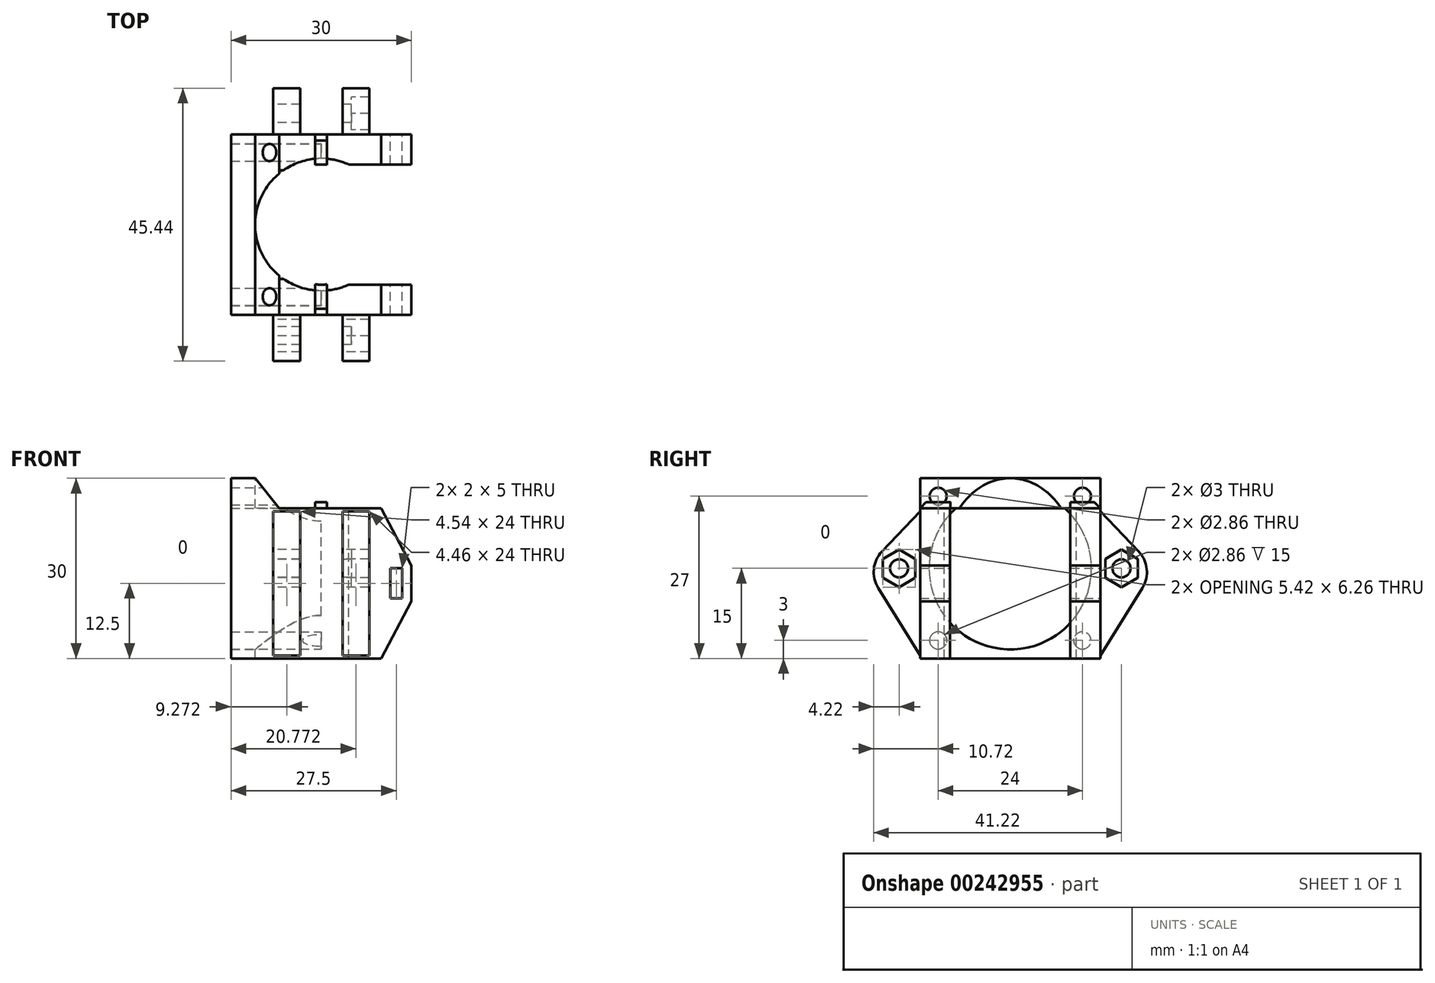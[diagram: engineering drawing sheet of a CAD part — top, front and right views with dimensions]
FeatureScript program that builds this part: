
annotation { "Feature Type Name" : "Feature", "Feature Type Description" : "" }
export const myFeature = defineFeature(function(context is Context, id is Id, definition is map)
    precondition{}
    {
        {
            var Q0;
            Q0=qCreatedBy(makeId("Front.planeOp"),FACE);
            var sketch = newSketch(context, id + "F0", { "sketchPlane" : qUnion([Q0])});
            skLineSegment(sketch, "E0", {"start": v(-15, 15) * mm, "end": v(-15, -15) * mm});
            skLineSegment(sketch, "E1", {"start": v(-15, -15) * mm, "end": v(10, -15) * mm});
            skLineSegment(sketch, "E2", {"start": v(15, -5.5) * mm, "end": v(15, 0.5) * mm});
            skLineSegment(sketch, "E3", {"start": v(10, 10) * mm, "end": v(-7, 10) * mm});
            skLineSegment(sketch, "E4", {"start": v(-11, 15) * mm, "end": v(-15, 15) * mm});
            skLineSegment(sketch, "E5.0", {"start": v(10, -15) * mm, "end": v(10, 10) * mm});
            skLineSegment(sketch, "E6", {"start": v(10, 10) * mm, "end": v(15, 0.5) * mm});
            skLineSegment(sketch, "E7", {"start": v(15, -5.5) * mm, "end": v(10, -15) * mm});
            skLineSegment(sketch, "E8.0", {"start": v(13.5, -5) * mm, "end": v(13.5, 0) * mm});
            skLineSegment(sketch, "E9.0", {"start": v(11.5, -5) * mm, "end": v(11.5, 0) * mm});
            skLineSegment(sketch, "E10.trimOffspring", {"start": v(11.5, 0) * mm, "end": v(13.5, 0) * mm});
            skLineSegment(sketch, "E11.trimOffspring", {"start": v(11.5, -5) * mm, "end": v(13.5, -5) * mm});
            skLineSegment(sketch, "E12", {"start": v(-11, 15) * mm, "end": v(-7, 10) * mm});
            skSolve(sketch);
        }
        {
            var Q0;
            Q0=qCreatedBy(makeId("Top.planeOp"),FACE);
            var sketch = newSketch(context, id + "F1", { "sketchPlane" : qUnion([Q0])});
            skArc(sketch, "E13", {"start": v(4.58, 10) * mm, "mid": v(-11, 0) * mm, "end": v(4.58, -10) * mm});
            skLineSegment(sketch, "E14.0", {"start": v(4.58, -10) * mm, "end": v(16, -10) * mm});
            skLineSegment(sketch, "E15.0", {"start": v(4.58, 10) * mm, "end": v(16, 10) * mm});
            skLineSegment(sketch, "E16", {"start": v(16, 10) * mm, "end": v(16, -10) * mm});
            skSolve(sketch);
        }
        {
            var Q0;
            Q0=qCreatedBy(makeId("Right.planeOp"),FACE);
            var sketch = newSketch(context, id + "F2", { "sketchPlane" : qUnion([Q0])});
            skArc(sketch, "E17", {"start": v(-9.07, 10) * mm, "mid": v(0, -13.5) * mm, "end": v(9.07, 10) * mm});
            skLineSegment(sketch, "E18", {"start": v(-9.07, 10) * mm, "end": v(9.07, 10) * mm});
            skCircle(sketch, "E19", {"center": v(-12, -12) * mm, "radius": 1.43 * mm});
            skCircle(sketch, "E20", {"center": v(-12, 12) * mm, "radius": 1.43 * mm});
            skCircle(sketch, "E21", {"center": v(12, -12) * mm, "radius": 1.43 * mm});
            skCircle(sketch, "E22", {"center": v(12, 12) * mm, "radius": 1.43 * mm});
            skSolve(sketch);
        }
        {
            var Q0;
            Q0=qCreatedBy(makeId("Right.planeOp"),FACE);
            var sketch = newSketch(context, id + "F3", { "sketchPlane" : qUnion([Q0])});
            skLineSegment(sketch, "E23", {"start": v(21.97, -3.26) * mm, "end": v(15, -14.5) * mm});
            skLineSegment(sketch, "E24", {"start": v(21.34, 2.81) * mm, "end": v(15, 9.5) * mm});
            skLineSegment(sketch, "E25", {"start": v(15, 9.5) * mm, "end": v(15, -14.5) * mm});
            skCircle(sketch, "E26", {"center": v(18.5, 0) * mm, "radius": 1.5 * mm});
            skPoint(sketch, "E27.visualSharp", {"position": v(24, 0.02) * mm});
            skArc(sketch, "E27.filletArc", {"start": v(21.97, -3.26) * mm, "mid": v(22.7, -0.12) * mm, "end": v(21.34, 2.81) * mm});
            skLineSegment(sketch, "E28.MirrorCS", {"start": v(-21.34, 2.81) * mm, "end": v(-15, 9.5) * mm});
            skArc(sketch, "E29.MirrorCS", {"start": v(-21.97, -3.26) * mm, "mid": v(-22.7, -0.12) * mm, "end": v(-21.34, 2.81) * mm});
            skLineSegment(sketch, "E30.MirrorCS", {"start": v(-21.97, -3.26) * mm, "end": v(-15, -14.5) * mm});
            skCircle(sketch, "E31.MirrorC", {"center": v(-18.5, 0) * mm, "radius": 1.5 * mm});
            skLineSegment(sketch, "E32.MirrorCS", {"start": v(-15, 9.5) * mm, "end": v(-15, -14.5) * mm});
            skPoint(sketch, "E33.0.midPoint", {"position": v(18.5, 2.5) * mm});
            skCircle(sketch, "E34.cCircle", {"center": v(18.5, 0) * mm, "radius": 2.71 * mm, "construction": true});
            skLineSegment(sketch, "E34.0", {"start": v(21.2, 1.56) * mm, "end": v(21.2, -1.56) * mm});
            skLineSegment(sketch, "E34.1", {"start": v(21.2, -1.56) * mm, "end": v(18.5, -3.13) * mm});
            skLineSegment(sketch, "E34.2", {"start": v(18.5, -3.13) * mm, "end": v(15.8, -1.56) * mm});
            skLineSegment(sketch, "E34.3", {"start": v(15.8, -1.56) * mm, "end": v(15.8, 1.56) * mm});
            skLineSegment(sketch, "E34.4", {"start": v(15.8, 1.56) * mm, "end": v(18.5, 3.13) * mm});
            skLineSegment(sketch, "E34.5", {"start": v(18.5, 3.13) * mm, "end": v(21.2, 1.56) * mm});
            skPoint(sketch, "E34.0.midPoint", {"position": v(21.2, 0) * mm});
            skCircle(sketch, "E35.MirrorC", {"center": v(-18.5, 0) * mm, "radius": 2.71 * mm, "construction": true});
            skLineSegment(sketch, "E36.MirrorCS", {"start": v(-18.5, 3.13) * mm, "end": v(-21.2, 1.56) * mm});
            skLineSegment(sketch, "E37.MirrorCS", {"start": v(-21.2, 1.56) * mm, "end": v(-21.2, -1.56) * mm});
            skLineSegment(sketch, "E38.MirrorCS", {"start": v(-21.2, -1.56) * mm, "end": v(-18.5, -3.13) * mm});
            skLineSegment(sketch, "E39.MirrorCS", {"start": v(-18.5, -3.13) * mm, "end": v(-15.8, -1.56) * mm});
            skLineSegment(sketch, "E40.MirrorCS", {"start": v(-15.8, -1.56) * mm, "end": v(-15.8, 1.56) * mm});
            skLineSegment(sketch, "E41.MirrorCS", {"start": v(-15.8, 1.56) * mm, "end": v(-18.5, 3.13) * mm});
            skSolve(sketch);
        }
        {
            var Q0;
            Q0=qCreatedBy(makeId("Top.planeOp"),FACE);
            var sketch = newSketch(context, id + "F4", { "sketchPlane" : qUnion([Q0])});
            skLineSegment(sketch, "E42", {"start": v(3.54, 15) * mm, "end": v(3.54, 27) * mm});
            skLineSegment(sketch, "E43", {"start": v(3.54, 27) * mm, "end": v(-3.46, 27) * mm});
            skLineSegment(sketch, "E44", {"start": v(-3.46, 27) * mm, "end": v(-3.46, 15) * mm});
            skLineSegment(sketch, "E45", {"start": v(-3.46, 15) * mm, "end": v(3.54, 15) * mm});
            skLineSegment(sketch, "E46.MirrorCS", {"start": v(3.54, -27) * mm, "end": v(-3.46, -27) * mm});
            skLineSegment(sketch, "E47.MirrorCS", {"start": v(3.54, -15) * mm, "end": v(3.54, -27) * mm});
            skLineSegment(sketch, "E48.MirrorCS", {"start": v(-3.46, -27) * mm, "end": v(-3.46, -15) * mm});
            skLineSegment(sketch, "E49.MirrorCS", {"start": v(-3.46, -15) * mm, "end": v(3.54, -15) * mm});
            skSolve(sketch);
        }
        {
            var Q0;
            Q0=makeQuery(id+"F0.imprint","IMPRINT",FACE,{"disambiguationData":[TD([[makeQuery(id+"F0.imprint","IMPRINT",EDGE,{"derivedFrom":sQuery(id+"F0.wireOp",EDGE,"E0")}),1.0]])]});
            var Q1;
            Q1=makeQuery(id+"F0.imprint","IMPRINT",FACE,{"disambiguationData":[TD([[makeQuery(id+"F0.imprint","IMPRINT",EDGE,{"derivedFrom":sQuery(id+"F0.wireOp",EDGE,"E2")}),1.0]])]});
            extrude(context, id + "F5", {"entities" : qUnion([Q0, Q1]), "endBound" : BoundingType.SYMMETRIC, "offsetDistance" : 25 * mm, "depth" : 30 * mm});
        }
        {
            var Q0;
            Q0=makeQuery(id+"F1.imprint","IMPRINT",FACE,{"disambiguationData":[TD([[makeQuery(id+"F1.imprint","IMPRINT",EDGE,{"derivedFrom":sQuery(id+"F1.wireOp",EDGE,"E13")}),1.0]])]});
            extrude(context, id + "F6", {"entities" : qUnion([Q0]), "operationType" : NewBodyOperationType.REMOVE, "endBound" : BoundingType.SYMMETRIC, "oppositeDirection" : true, "depth" : 30 * mm});
        }
        {
            var Q0;
            Q0=makeQuery(id+"F2.imprint","IMPRINT",FACE,{"disambiguationData":[TD([[makeQuery(id+"F2.imprint","IMPRINT",EDGE,{"derivedFrom":sQuery(id+"F2.wireOp",EDGE,"E17")}),1.0]])]});
            extrude(context, id + "F7", {"entities" : qUnion([Q0]), "operationType" : NewBodyOperationType.REMOVE, "oppositeDirection" : true, "depth" : 16 * mm});
        }
        {
            var Q0;
            Q0=makeQuery(id+"F2.imprint","IMPRINT",FACE,{"disambiguationData":[TD([[makeQuery(id+"F2.imprint","IMPRINT",EDGE,{"derivedFrom":sQuery(id+"F2.wireOp",EDGE,"E22")}),1.0]])]});
            var Q1;
            Q1=makeQuery(id+"F2.imprint","IMPRINT",FACE,{"disambiguationData":[TD([[makeQuery(id+"F2.imprint","IMPRINT",EDGE,{"derivedFrom":sQuery(id+"F2.wireOp",EDGE,"E20")}),1.0]])]});
            extrude(context, id + "F8", {"entities" : qUnion([Q0, Q1]), "operationType" : NewBodyOperationType.REMOVE, "oppositeDirection" : true, "depth" : 25 * mm});
        }
        {
            var Q0;
            Q0=makeQuery(id+"F2.imprint","IMPRINT",FACE,{"disambiguationData":[TD([[makeQuery(id+"F2.imprint","IMPRINT",EDGE,{"derivedFrom":sQuery(id+"F2.wireOp",EDGE,"E21")}),1.0]])]});
            var Q1;
            Q1=makeQuery(id+"F2.imprint","IMPRINT",FACE,{"disambiguationData":[TD([[makeQuery(id+"F2.imprint","IMPRINT",EDGE,{"derivedFrom":sQuery(id+"F2.wireOp",EDGE,"E19")}),1.0]])]});
            extrude(context, id + "F9", {"entities" : qUnion([Q0, Q1]), "operationType" : NewBodyOperationType.REMOVE, "oppositeDirection" : true, "depth" : 25 * mm});
        }
        {
            var Q0;
            Q0=makeQuery(id+"F3.imprint","IMPRINT",FACE,{"disambiguationData":[TD([[makeQuery(id+"F3.imprint","IMPRINT",EDGE,{"derivedFrom":sQuery(id+"F3.wireOp",EDGE,"E23")}),-1.0]])]});
            var Q1;
            Q1=makeQuery(id+"F3.imprint","IMPRINT",FACE,{"disambiguationData":[TD([[makeQuery(id+"F3.imprint","IMPRINT",EDGE,{"derivedFrom":sQuery(id+"F3.wireOp",EDGE,"E26")}),-1.0]])]});
            var Q2;
            Q2=makeQuery(id+"F3.imprint","IMPRINT",FACE,{"disambiguationData":[TD([[makeQuery(id+"F3.imprint","IMPRINT",EDGE,{"derivedFrom":sQuery(id+"F3.wireOp",EDGE,"E28.MirrorCS")}),-1.0]])]});
            var Q3;
            Q3=makeQuery(id+"F3.imprint","IMPRINT",FACE,{"disambiguationData":[TD([[makeQuery(id+"F3.imprint","IMPRINT",EDGE,{"derivedFrom":sQuery(id+"F3.wireOp",EDGE,"E31.MirrorC")}),1.0]])]});
            extrude(context, id + "F10", {"entities" : qUnion([Q0, Q1, Q2, Q3]), "operationType" : NewBodyOperationType.ADD, "endBound" : BoundingType.SYMMETRIC, "depth" : 16 * mm});
        }
        {
            var Q0;
            Q0=makeQuery(id+"F3.imprint","IMPRINT",FACE,{"disambiguationData":[TD([[makeQuery(id+"F3.imprint","IMPRINT",EDGE,{"derivedFrom":sQuery(id+"F3.wireOp",EDGE,"E26")}),-1.0]])]});
            var Q1;
            Q1=makeQuery(id+"F3.imprint","IMPRINT",FACE,{"disambiguationData":[TD([[makeQuery(id+"F3.imprint","IMPRINT",EDGE,{"derivedFrom":sQuery(id+"F3.wireOp",EDGE,"E26")}),1.0]])]});
            var Q2;
            Q2=makeQuery(id+"F3.imprint","IMPRINT",FACE,{"disambiguationData":[TD([[makeQuery(id+"F3.imprint","IMPRINT",EDGE,{"derivedFrom":sQuery(id+"F3.wireOp",EDGE,"E31.MirrorC")}),1.0]])]});
            var Q3;
            Q3=makeQuery(id+"F3.imprint","IMPRINT",FACE,{"disambiguationData":[TD([[makeQuery(id+"F3.imprint","IMPRINT",EDGE,{"derivedFrom":sQuery(id+"F3.wireOp",EDGE,"E31.MirrorC")}),-1.0]])]});
            extrude(context, id + "F11", {"entities" : qUnion([Q0, Q1, Q2, Q3]), "operationType" : NewBodyOperationType.REMOVE, "depth" : 25 * mm, "hasSecondDirection" : true, "secondDirectionOppositeDirection" : false, "secondDirectionDepth" : 5 * mm});
        }
        {
            var Q0;
            Q0=makeQuery(id+"F4.imprint","IMPRINT",FACE,{"disambiguationData":[TD([[makeQuery(id+"F4.imprint","IMPRINT",EDGE,{"derivedFrom":sQuery(id+"F4.wireOp",EDGE,"E42")}),1.0]])]});
            var Q1;
            Q1=makeQuery(id+"F4.imprint","IMPRINT",FACE,{"disambiguationData":[TD([[makeQuery(id+"F4.imprint","IMPRINT",EDGE,{"derivedFrom":sQuery(id+"F4.wireOp",EDGE,"E46.MirrorCS")}),-1.0]])]});
            extrude(context, id + "F12", {"entities" : qUnion([Q0, Q1]), "operationType" : NewBodyOperationType.REMOVE, "endBound" : BoundingType.SYMMETRIC, "depth" : 40 * mm});
        }
        {
            var Q0;
            Q0=qCreatedBy(makeId("Top.planeOp"),FACE);
            var sketch = newSketch(context, id + "F13", { "sketchPlane" : qUnion([Q0])});
            skLineSegment(sketch, "E50.bottom", {"start": v(-1.01, 15) * mm, "end": v(0.99, 15) * mm});
            skLineSegment(sketch, "E50.top", {"start": v(-1.01, -15) * mm, "end": v(0.99, -15) * mm});
            skLineSegment(sketch, "E50.left", {"start": v(-1.01, 15) * mm, "end": v(-1.01, -15) * mm});
            skLineSegment(sketch, "E50.right", {"start": v(0.99, 15) * mm, "end": v(0.99, -15) * mm});
            skSolve(sketch);
        }
        {
            var Q0;
            Q0=makeQuery(id+"F13.imprint","IMPRINT",FACE,{"disambiguationData":[TD([[makeQuery(id+"F13.imprint","IMPRINT",EDGE,{"derivedFrom":sQuery(id+"F13.wireOp",EDGE,"E50.bottom")}),-1.0]])]});
            extrude(context, id + "F14", {"entities" : qUnion([Q0]), "operationType" : NewBodyOperationType.ADD, "depth" : 11 * mm, "hasSecondDirection" : true, "secondDirectionOppositeDirection" : false, "secondDirectionDepth" : 10 * mm});
        }
        {
            var Q0;
            Q0=qCreatedBy(makeId("Top.planeOp"),FACE);
            var sketch = newSketch(context, id + "F15", { "sketchPlane" : qUnion([Q0])});
            skCircle(sketch, "E51", {"center": v(0, 0) * mm, "radius": 10 * mm});
            skSolve(sketch);
        }
        {
            var Q0;
            Q0=makeQuery(id+"F15.imprint","IMPRINT",FACE,{"disambiguationData":[TD([[makeQuery(id+"F15.imprint","IMPRINT",EDGE,{"derivedFrom":sQuery(id+"F15.wireOp",EDGE,"E51")}),1.0]])]});
            extrude(context, id + "F16", {"entities" : qUnion([Q0]), "operationType" : NewBodyOperationType.REMOVE, "depth" : 25 * mm});
        }
        {
            var Q0;
            {var subQ0=sQuery(id+"F13.wireOp",EDGE,"E50.right");Q0=makeQuery(id+"F16.boolean.opBoolean","SPLIT",EDGE,{"disambiguationData":[TD([makeQuery(id+"F12.opExtrude","SWEPT_FACE",FACE,{"disambiguationData":[OSD([sQuery(id+"F4.wireOp",EDGE,"E45")])]})])],"derivedFrom":makeQuery(id+"F14.opExtrude","CAP_EDGE",EDGE,{"disambiguationData":[OSD([subQ0])],"isStart":false})});}
            var Q1;
            {var subQ0=sQuery(id+"F13.wireOp",EDGE,"E50.left");Q1=makeQuery(id+"F16.boolean.opBoolean","SPLIT",EDGE,{"disambiguationData":[TD([makeQuery(id+"F12.opExtrude","SWEPT_FACE",FACE,{"disambiguationData":[OSD([sQuery(id+"F4.wireOp",EDGE,"E45")])]})])],"derivedFrom":makeQuery(id+"F14.opExtrude","CAP_EDGE",EDGE,{"disambiguationData":[OSD([subQ0])],"isStart":false})});}
            var Q2;
            Q2=makeQuery(id+"F14.opExtrude","CAP_EDGE",EDGE,{"disambiguationData":[OSD([sQuery(id+"F13.wireOp",EDGE,"E50.bottom")])],"isStart":false});
            var Q3;
            {var subQ1=sQuery(id+"F13.wireOp",EDGE,"E50.right");Q3=makeQuery(id+"F16.boolean.opBoolean","SPLIT",EDGE,{"disambiguationData":[TD([makeQuery(id+"F12.opExtrude","SWEPT_FACE",FACE,{"disambiguationData":[OSD([sQuery(id+"F4.wireOp",EDGE,"E49.MirrorCS")])]})])],"derivedFrom":makeQuery(id+"F14.opExtrude","CAP_EDGE",EDGE,{"disambiguationData":[OSD([subQ1])],"isStart":false})});}
            var Q4;
            Q4=makeQuery(id+"F14.opExtrude","CAP_EDGE",EDGE,{"disambiguationData":[OSD([sQuery(id+"F13.wireOp",EDGE,"E50.top")])],"isStart":false});
            var Q5;
            {var subQ1=sQuery(id+"F13.wireOp",EDGE,"E50.left");Q5=makeQuery(id+"F16.boolean.opBoolean","SPLIT",EDGE,{"disambiguationData":[TD([makeQuery(id+"F12.opExtrude","SWEPT_FACE",FACE,{"disambiguationData":[OSD([sQuery(id+"F4.wireOp",EDGE,"E49.MirrorCS")])]})])],"derivedFrom":makeQuery(id+"F14.opExtrude","CAP_EDGE",EDGE,{"disambiguationData":[OSD([subQ1])],"isStart":false})});}
            chamfer(context, id + "F17", {"entities" : qUnion([Q0, Q1, Q2, Q3, Q4, Q5]), "width" : 1 * mm, "tangentPropagation" : true});
        }
    });
